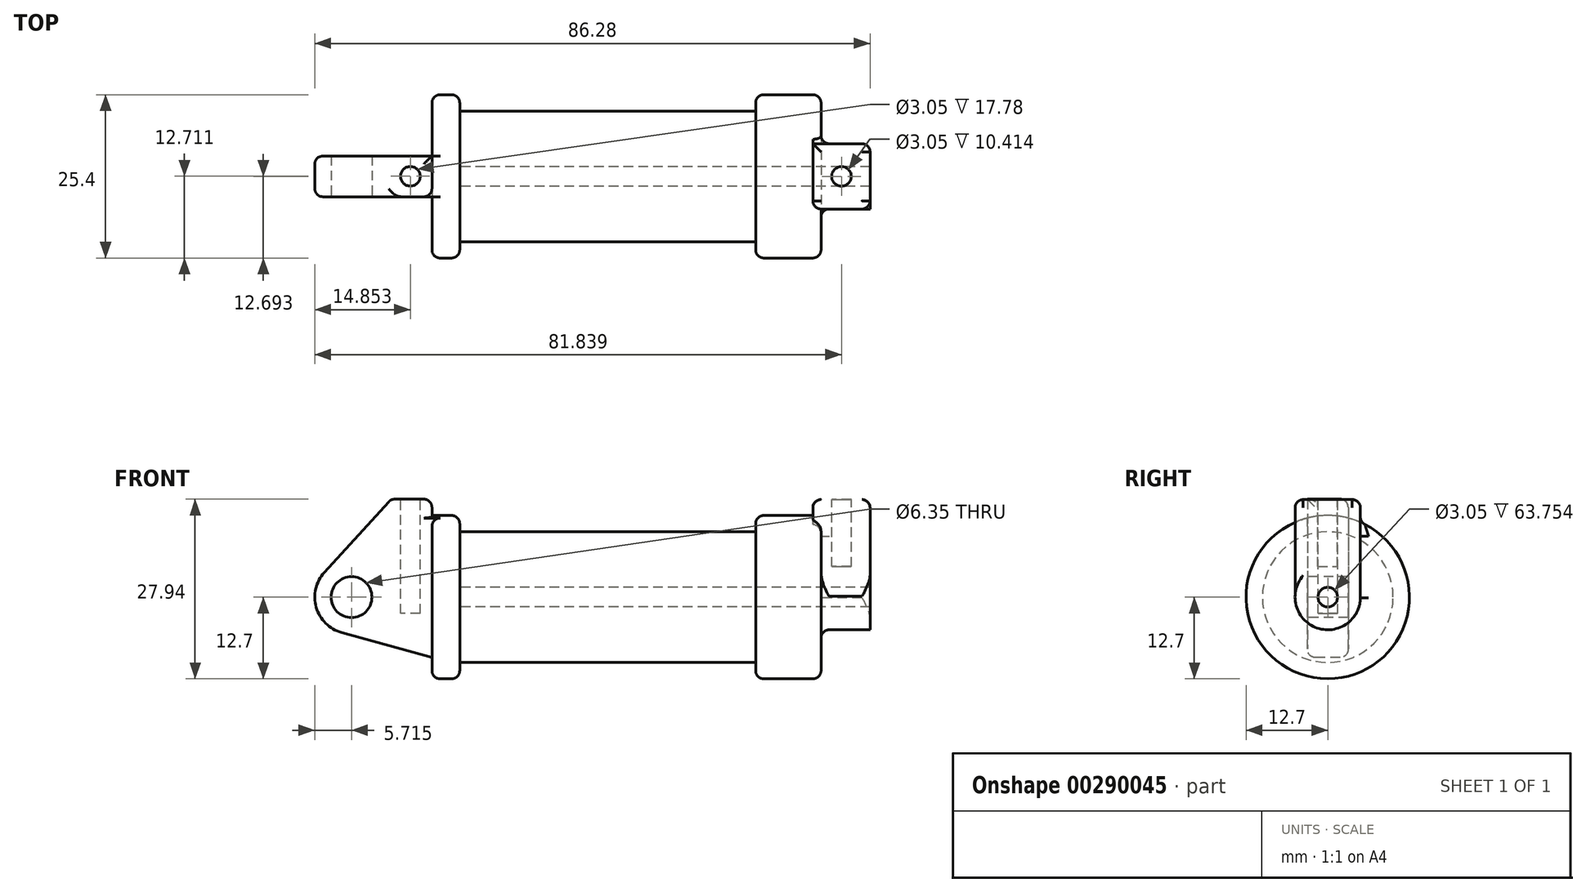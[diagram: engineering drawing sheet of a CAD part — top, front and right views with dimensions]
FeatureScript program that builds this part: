
annotation { "Feature Type Name" : "Feature", "Feature Type Description" : "" }
export const myFeature = defineFeature(function(context is Context, id is Id, definition is map)
    precondition{}
    {
        {
            var Q0;
            Q0=qCreatedBy(makeId("Front.planeOp"),FACE);
            var sketch = newSketch(context, id + "F0", { "sketchPlane" : qUnion([Q0])});
            skLineSegment(sketch, "E0", {"start": v(0, 0) * mm, "end": v(0, 12.7) * mm});
            skLineSegment(sketch, "E1", {"start": v(0, 12.7) * mm, "end": v(10.16, 12.7) * mm});
            skLineSegment(sketch, "E2", {"start": v(10.16, 12.7) * mm, "end": v(10.16, 10.16) * mm});
            skLineSegment(sketch, "E3", {"start": v(10.16, 10.16) * mm, "end": v(56.13, 10.16) * mm});
            skLineSegment(sketch, "E4", {"start": v(56.13, 10.16) * mm, "end": v(56.13, 12.7) * mm});
            skLineSegment(sketch, "E5", {"start": v(56.13, 12.7) * mm, "end": v(66.3, 12.7) * mm});
            skLineSegment(sketch, "E6", {"start": v(66.3, 12.7) * mm, "end": v(66.3, 0) * mm});
            skLineSegment(sketch, "E7", {"start": v(66.3, 0) * mm, "end": v(0, 0) * mm});
            skLineSegment(sketch, "E8", {"start": v(5.84, 15.24) * mm, "end": v(-0.5, 15.24) * mm});
            skLineSegment(sketch, "E9", {"start": v(-0.5, 15.24) * mm, "end": v(-10.88, 3.85) * mm});
            skLineSegment(sketch, "E10", {"start": v(0, 0) * mm, "end": v(-6.65, 0) * mm});
            skCircle(sketch, "E11", {"center": v(-6.65, 0) * mm, "radius": 5.72 * mm});
            skCircle(sketch, "E12", {"center": v(-6.65, 0) * mm, "radius": 3.18 * mm});
            skLineSegment(sketch, "E13", {"start": v(5.84, 15.24) * mm, "end": v(5.84, -9.4) * mm});
            skLineSegment(sketch, "E14", {"start": v(5.84, -9.4) * mm, "end": v(-8.18, -5.5) * mm});
            skSolve(sketch);
        }
        {
            var Q0;
            {var subQ0=sQuery(id+"F0.wireOp",EDGE,"E2");Q0=makeQuery(id+"F0.imprint","IMPRINT",FACE,{"disambiguationData":[TD([[makeQuery(id+"F0.imprint","IMPRINT",EDGE,{"derivedFrom":subQ0}),-1.0]])]});}
            var Q1;
            Q1=sQuery(id+"F0.wireOp",EDGE,"E7");
            revolve(context, id + "F1", {"entities" : qUnion([Q0]), "axis" : qUnion([Q1]), "revolveType" : RevolveType.FULL});
        }
        {
            var Q0;
            {var subQ1=sQuery(id+"F0.wireOp",EDGE,"E0");Q0=makeQuery(id+"F0.imprint","IMPRINT",FACE,{"disambiguationData":[TD([[makeQuery(id+"F0.imprint","IMPRINT",EDGE,{"derivedFrom":subQ1}),1.0]])]});}
            var Q1;
            {var subQ0=sQuery(id+"F0.wireOp",EDGE,"E0");Q1=makeQuery(id+"F0.imprint","IMPRINT",FACE,{"disambiguationData":[TD([[makeQuery(id+"F0.imprint","IMPRINT",EDGE,{"derivedFrom":subQ0}),-1.0]])]});}
            var Q2;
            {var subQ0=sQuery(id+"F0.wireOp",EDGE,"E14");Q2=makeQuery(id+"F0.imprint","IMPRINT",FACE,{"disambiguationData":[TD([[makeQuery(id+"F0.imprint","IMPRINT",EDGE,{"derivedFrom":subQ0}),-1.0]])]});}
            var Q3;
            {var subQ5=sQuery(id+"F0.wireOp",EDGE,"E12");Q3=makeQuery(id+"F0.imprint","IMPRINT",FACE,{"disambiguationData":[TD([[makeQuery(id+"F0.imprint","IMPRINT",EDGE,{"derivedFrom":subQ5}),-1.0]])]});}
            extrude(context, id + "F2", {"entities" : qUnion([Q0, Q1, Q2, Q3]), "operationType" : NewBodyOperationType.ADD, "endBound" : BoundingType.SYMMETRIC, "oppositeDirection" : true, "depth" : 6.35 * mm});
        }
        {
            var Q0;
            Q0=makeQuery(id+"F1.opRevolve","SWEPT_FACE",FACE,{"disambiguationData":[OSD([sQuery(id+"F0.wireOp",EDGE,"E6")])]});
            var sketch = newSketch(context, id + "F3", { "sketchPlane" : qUnion([Q0])});
            skCircle(sketch, "E15", {"center": v(0, 0) * mm, "radius": 5.08 * mm});
            skLineSegment(sketch, "E16", {"start": v(5.08, -0.1) * mm, "end": v(5.08, 15.16) * mm});
            skLineSegment(sketch, "E17", {"start": v(-5.08, 0.12) * mm, "end": v(-5.08, 15.17) * mm});
            skLineSegment(sketch, "E18", {"start": v(-5.08, 15.17) * mm, "end": v(5.08, 15.16) * mm});
            skCircle(sketch, "E19", {"center": v(0, 0) * mm, "radius": 1.52 * mm});
            skSolve(sketch);
        }
        {
            var Q0;
            {var subQ0=sQuery(id+"F3.wireOp",EDGE,"E17");var subQ1=sQuery(id+"F3.wireOp",EDGE,"E15");var subQ2=makeQuery(id+"F3.imprint","INTERSECT",VERTEX,{"derivedFrom":[subQ1,subQ0]});Q0=makeQuery(id+"F3.imprint","IMPRINT",FACE,{"disambiguationData":[TD([[makeQuery(id+"F3.imprint","IMPRINT",EDGE,{"disambiguationData":[TD([[subQ2,1.0]])],"derivedFrom":subQ1}),-1.0]])]});}
            var Q1;
            {var subQ0=sQuery(id+"F3.wireOp",EDGE,"E18");Q1=makeQuery(id+"F3.imprint","IMPRINT",FACE,{"disambiguationData":[TD([[makeQuery(id+"F3.imprint","IMPRINT",EDGE,{"derivedFrom":subQ0}),-1.0]])]});}
            var Q2;
            Q2=makeQuery(id+"F3.imprint","IMPRINT",FACE,{"disambiguationData":[TD([[makeQuery(id+"F3.imprint","IMPRINT",EDGE,{"derivedFrom":sQuery(id+"F3.wireOp",EDGE,"E19")}),-1.0]])]});
            extrude(context, id + "F4", {"entities" : qUnion([Q0, Q1, Q2]), "operationType" : NewBodyOperationType.ADD, "depth" : 7.62 * mm});
        }
        {
            var Q0;
            Q0=makeQuery(id+"F4.opExtrude","CAP_FACE",FACE,{"disambiguationData":[OSD([sQuery(id+"F3.wireOp",EDGE,"E15"),sQuery(id+"F3.wireOp",EDGE,"E16"),sQuery(id+"F3.wireOp",EDGE,"E17"),sQuery(id+"F3.wireOp",EDGE,"E18"),sQuery(id+"F3.wireOp",EDGE,"E19")])],"isStart":true});
            extrude(context, id + "F5", {"entities" : qUnion([Q0]), "operationType" : NewBodyOperationType.ADD, "depth" : 1.27 * mm});
        }
        {
            var Q0;
            Q0=makeQuery(id+"F4.boolean.opBoolean","SPLIT",FACE,{"disambiguationData":[TD([makeQuery(id+"F4.opExtrude","SWEPT_FACE",FACE,{"disambiguationData":[OSD([sQuery(id+"F3.wireOp",EDGE,"E19")])]})])],"derivedFrom":makeQuery(id+"F1.opRevolve","SWEPT_FACE",FACE,{"disambiguationData":[OSD([sQuery(id+"F0.wireOp",EDGE,"E6")])]})});
            var Q1;
            Q1=makeQuery(id+"F1.opRevolve","SWEPT_FACE",FACE,{"disambiguationData":[OSD([sQuery(id+"F0.wireOp",EDGE,"E2")])]});
            extrude(context, id + "F6", {"entities" : qUnion([Q0]), "operationType" : NewBodyOperationType.REMOVE, "endBound" : BoundingType.UP_TO_SURFACE, "oppositeDirection" : true, "endBoundEntityFace" : qUnion([Q1]), "depth" : 25.4 * mm});
        }
        {
            var Q0;
            {var subQ0=sQuery(id+"F3.wireOp",EDGE,"E18");Q0=makeQuery(id+"F5.boolean.opBoolean","MERGE",FACE,{"derivedFrom":[makeQuery(id+"F4.opExtrude","SWEPT_FACE",FACE,{"disambiguationData":[OSD([subQ0])]}),makeQuery(id+"F5.opExtrude","SWEPT_FACE",FACE,{"disambiguationData":[OSD([subQ0])]})]});}
            var sketch = newSketch(context, id + "F7", { "sketchPlane" : qUnion([Q0])});
            skCircle(sketch, "E20", {"center": v(69.47, -0.02) * mm, "radius": 1.52 * mm});
            skSolve(sketch);
        }
        {
            var Q0;
            Q0=makeQuery(id+"F2.opExtrude","SWEPT_FACE",FACE,{"disambiguationData":[OSD([sQuery(id+"F0.wireOp",EDGE,"E8")])]});
            var sketch = newSketch(context, id + "F8", { "sketchPlane" : qUnion([Q0])});
            skCircle(sketch, "E21", {"center": v(2.48, 0.01) * mm, "radius": 1.52 * mm});
            skSolve(sketch);
        }
        {
            var Q0;
            Q0=makeQuery(id+"F8.imprint","IMPRINT",FACE,{"disambiguationData":[TD([[makeQuery(id+"F8.imprint","IMPRINT",EDGE,{"derivedFrom":sQuery(id+"F8.wireOp",EDGE,"E21")}),1.0]])]});
            var Q1;
            Q1 = qSketchRegion(id + "F8", true);
            extrude(context, id + "F9", {"entities" : qUnion([Q0, Q1]), "operationType" : NewBodyOperationType.REMOVE, "oppositeDirection" : true, "depth" : 17.78 * mm});
        }
        {
            var Q0;
            Q0=makeQuery(id+"F7.imprint","IMPRINT",FACE,{"disambiguationData":[TD([[makeQuery(id+"F7.imprint","IMPRINT",EDGE,{"derivedFrom":sQuery(id+"F7.wireOp",EDGE,"E20")}),1.0]])]});
            extrude(context, id + "F10", {"entities" : qUnion([Q0]), "operationType" : NewBodyOperationType.REMOVE, "oppositeDirection" : true, "depth" : 10.4 * mm});
        }
        {
            var Q0;
            {var subQ0=sQuery(id+"F0.wireOp",EDGE,"E5");var subQ1=sQuery(id+"F0.wireOp",EDGE,"E6");Q0=makeQuery(id+"F4.boolean.opBoolean","SPLIT",EDGE,{"disambiguationData":[topologyDisambiguationEdgeConnected([makeQuery(id+"F1.opRevolve","SWEPT_FACE",FACE,{"disambiguationData":[OSD([subQ1])]})])],"derivedFrom":makeQuery(id+"F1.opRevolve","SWEPT_EDGE",EDGE,{"disambiguationData":[OSD([subQ0,subQ1])]})});}
            var Q1;
            Q1=makeQuery(id+"F1.opRevolve","SWEPT_EDGE",EDGE,{"disambiguationData":[OSD([sQuery(id+"F0.wireOp",EDGE,"E4"),sQuery(id+"F0.wireOp",EDGE,"E5")])]});
            var Q2;
            Q2=makeQuery(id+"F1.opRevolve","SWEPT_EDGE",EDGE,{"disambiguationData":[OSD([sQuery(id+"F0.wireOp",EDGE,"E1"),sQuery(id+"F0.wireOp",EDGE,"E2")])]});
            var Q3;
            {var subQ0=sQuery(id+"F0.wireOp",EDGE,"E1");var subQ1=sQuery(id+"F0.wireOp",EDGE,"E13");Q3=makeQuery(id+"F2.boolean.opBoolean","SPLIT",EDGE,{"disambiguationData":[topologyDisambiguationEdgeConnected([makeQuery(id+"F1.opRevolve","SWEPT_FACE",FACE,{"disambiguationData":[OSD([subQ1])]})])],"derivedFrom":makeQuery(id+"F1.opRevolve","SWEPT_EDGE",EDGE,{"disambiguationData":[OSD([subQ0,subQ1])]})});}
            var Q4;
            Q4=makeQuery(id+"F4.opExtrude","CAP_EDGE",EDGE,{"disambiguationData":[OSD([sQuery(id+"F3.wireOp",EDGE,"E18")])],"isStart":false});
            var Q5;
            {var subQ0=sQuery(id+"F3.wireOp",EDGE,"E18");var subQ1=sQuery(id+"F3.wireOp",EDGE,"E17");Q5=makeQuery(id+"F5.boolean.opBoolean","MERGE",EDGE,{"derivedFrom":[makeQuery(id+"F4.opExtrude","SWEPT_EDGE",EDGE,{"disambiguationData":[OSD([subQ1,subQ0])]}),makeQuery(id+"F5.opExtrude","SWEPT_EDGE",EDGE,{"disambiguationData":[OSD([subQ1,subQ0])]})]});}
            var Q6;
            {var subQ0=sQuery(id+"F3.wireOp",EDGE,"E18");var subQ1=sQuery(id+"F3.wireOp",EDGE,"E16");Q6=makeQuery(id+"F5.boolean.opBoolean","MERGE",EDGE,{"derivedFrom":[makeQuery(id+"F4.opExtrude","SWEPT_EDGE",EDGE,{"disambiguationData":[OSD([subQ1,subQ0])]}),makeQuery(id+"F5.opExtrude","SWEPT_EDGE",EDGE,{"disambiguationData":[OSD([subQ1,subQ0])]})]});}
            var Q7;
            Q7=makeQuery(id+"F5.opExtrude","CAP_EDGE",EDGE,{"disambiguationData":[OSD([sQuery(id+"F3.wireOp",EDGE,"E18")])],"isStart":false});
            fillet(context, id + "F11", {"entities" : qUnion([Q0, Q1, Q2, Q3, Q4, Q5, Q6, Q7]), "radius" : 1.27 * mm, "tangentPropagation" : true, "allowEdgeOverflow" : false});
        }
        {
            var Q0;
            Q0=makeQuery(id+"F5.opExtrude","CAP_EDGE",EDGE,{"disambiguationData":[OSD([sQuery(id+"F3.wireOp",EDGE,"E17")])],"isStart":false});
            var Q1;
            Q1=makeQuery(id+"F4.opExtrude","CAP_EDGE",EDGE,{"disambiguationData":[OSD([sQuery(id+"F3.wireOp",EDGE,"E17")])],"isStart":false});
            var Q2;
            Q2=makeQuery(id+"F2.opExtrude","CAP_EDGE",EDGE,{"disambiguationData":[OSD([sQuery(id+"F0.wireOp",EDGE,"E9")])],"isStart":false});
            var Q3;
            Q3=makeQuery(id+"F2.opExtrude","SWEPT_EDGE",EDGE,{"disambiguationData":[OSD([sQuery(id+"F0.wireOp",EDGE,"E8"),sQuery(id+"F0.wireOp",EDGE,"E9")])]});
            var Q4;
            Q4=makeQuery(id+"F2.opExtrude","CAP_EDGE",EDGE,{"disambiguationData":[OSD([sQuery(id+"F0.wireOp",EDGE,"E8")])],"isStart":false});
            var Q5;
            Q5=makeQuery(id+"F2.opExtrude","CAP_EDGE",EDGE,{"disambiguationData":[OSD([sQuery(id+"F0.wireOp",EDGE,"E9")])],"isStart":true});
            var Q6;
            {var subQ0=sQuery(id+"F0.wireOp",EDGE,"E13");Q6=makeQuery(id+"F2.boolean.opBoolean","SPLIT",EDGE,{"disambiguationData":[topologyDisambiguationEdgeConnected([makeQuery(id+"F2.opExtrude","SWEPT_FACE",FACE,{"disambiguationData":[OSD([subQ0])]})])],"derivedFrom":makeQuery(id+"F2.opExtrude","CAP_EDGE",EDGE,{"disambiguationData":[OSD([subQ0])],"isStart":true})});}
            var Q7;
            Q7=makeQuery(id+"F2.opExtrude","SWEPT_EDGE",EDGE,{"disambiguationData":[OSD([sQuery(id+"F0.wireOp",EDGE,"E8"),sQuery(id+"F0.wireOp",EDGE,"E13")])]});
            var Q8;
            Q8=makeQuery(id+"F4.opExtrude","CAP_EDGE",EDGE,{"disambiguationData":[OSD([sQuery(id+"F3.wireOp",EDGE,"E16")])],"isStart":false});
            var Q9;
            {var subQ0=sQuery(id+"F3.wireOp",EDGE,"E16");Q9=makeQuery(id+"F4.boolean.opBoolean","SPLIT",EDGE,{"disambiguationData":[topologyDisambiguationEdgeConnected([makeQuery(id+"F1.opRevolve","SWEPT_FACE",FACE,{"disambiguationData":[OSD([sQuery(id+"F0.wireOp",EDGE,"E6")])]})])],"derivedFrom":makeQuery(id+"F4.opExtrude","CAP_EDGE",EDGE,{"disambiguationData":[OSD([subQ0])],"isStart":true})});}
            fillet(context, id + "F12", {"entities" : qUnion([Q0, Q1, Q2, Q3, Q4, Q5, Q6, Q7, Q8, Q9]), "radius" : 1.27 * mm, "tangentPropagation" : true, "allowEdgeOverflow" : false});
        }
    });
